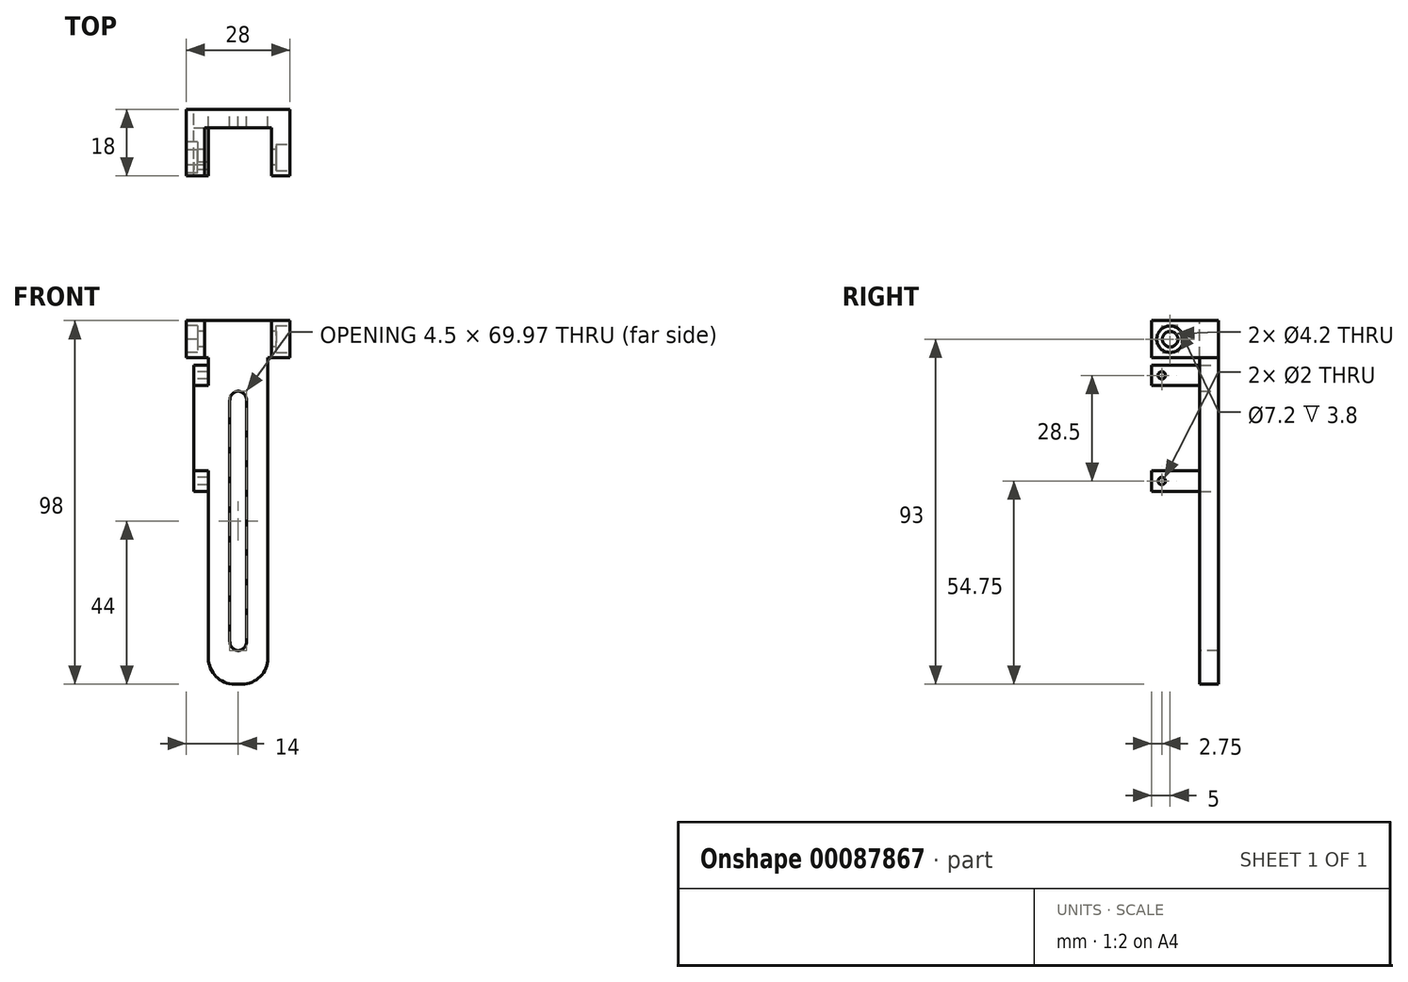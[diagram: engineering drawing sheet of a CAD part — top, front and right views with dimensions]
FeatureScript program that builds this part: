
annotation { "Feature Type Name" : "Feature", "Feature Type Description" : "" }
export const myFeature = defineFeature(function(context is Context, id is Id, definition is map)
    precondition{}
    {
        {
            var Q0;
            Q0=qCreatedBy(makeId("Front.planeOp"),FACE);
            var sketch = newSketch(context, id + "F0", { "sketchPlane" : qUnion([Q0])});
            skLineSegment(sketch, "E0.bottom", {"start": v(8, -44) * mm, "end": v(-8, -44) * mm});
            skLineSegment(sketch, "E0.top", {"start": v(8, 44) * mm, "end": v(-8, 44) * mm});
            skLineSegment(sketch, "E0.left", {"start": v(8, -44) * mm, "end": v(8, 44) * mm});
            skLineSegment(sketch, "E0.right", {"start": v(-8, -44) * mm, "end": v(-8, 44) * mm});
            skPoint(sketch, "E0.middle", {"position": v(0, 0) * mm});
            skLineSegment(sketch, "E1.bottom", {"start": v(-8, 42) * mm, "end": v(-12, 42) * mm});
            skLineSegment(sketch, "E1.top", {"start": v(-8, 8) * mm, "end": v(-12, 8) * mm});
            skLineSegment(sketch, "E1.left", {"start": v(-8, 42) * mm, "end": v(-8, 8) * mm});
            skLineSegment(sketch, "E1.right", {"start": v(-12, 42) * mm, "end": v(-12, 8) * mm});
            skLineSegment(sketch, "E2.bottom", {"start": v(14, 44) * mm, "end": v(8, 44) * mm});
            skLineSegment(sketch, "E2.top", {"start": v(14, 54) * mm, "end": v(-14, 54) * mm});
            skLineSegment(sketch, "E2.left", {"start": v(14, 44) * mm, "end": v(14, 54) * mm});
            skLineSegment(sketch, "E2.right", {"start": v(-14, 44) * mm, "end": v(-14, 54) * mm});
            skLineSegment(sketch, "E3.bottom", {"start": v(2.25, -35) * mm, "end": v(-2.25, -35) * mm});
            skLineSegment(sketch, "E3.top", {"start": v(2.25, 35) * mm, "end": v(-2.25, 35) * mm});
            skLineSegment(sketch, "E3.left", {"start": v(2.25, -35) * mm, "end": v(2.25, 35) * mm});
            skLineSegment(sketch, "E3.right", {"start": v(-2.25, -35) * mm, "end": v(-2.25, 35) * mm});
            skPoint(sketch, "E4", {"position": v(0, 54) * mm});
            skLineSegment(sketch, "E5.trimOffspring", {"start": v(-8, 44) * mm, "end": v(-14, 44) * mm});
            skSolve(sketch);
        }
        {
            var Q0;
            {var subQ1=sQuery(id+"F0.wireOp",EDGE,"E0.bottom");Q0=makeQuery(id+"F0.imprint","IMPRINT",FACE,{"disambiguationData":[TD([[makeQuery(id+"F0.imprint","IMPRINT",EDGE,{"derivedFrom":subQ1}),-1.0]])]});}
            var Q1;
            Q1=makeQuery(id+"F0.imprint","IMPRINT",FACE,{"disambiguationData":[TD([[makeQuery(id+"F0.imprint","IMPRINT",EDGE,{"derivedFrom":sQuery(id+"F0.wireOp",EDGE,"E0.top")}),-1.0]])]});
            var Q2;
            Q2=makeQuery(id+"F0.imprint","IMPRINT",FACE,{"disambiguationData":[TD([[makeQuery(id+"F0.imprint","IMPRINT",EDGE,{"derivedFrom":sQuery(id+"F0.wireOp",EDGE,"E1.bottom")}),1.0]])]});
            extrude(context, id + "F1", {"entities" : qUnion([Q0, Q1, Q2]), "depth" : 5 * mm});
        }
        {
            var Q0;
            Q0=makeQuery(id+"F1.opExtrude","CAP_FACE",FACE,{"disambiguationData":[OSD([sQuery(id+"F0.wireOp",EDGE,"E0.bottom"),sQuery(id+"F0.wireOp",EDGE,"E0.left"),sQuery(id+"F0.wireOp",EDGE,"E0.right"),sQuery(id+"F0.wireOp",EDGE,"E1.bottom"),sQuery(id+"F0.wireOp",EDGE,"E1.top"),sQuery(id+"F0.wireOp",EDGE,"E1.right"),sQuery(id+"F0.wireOp",EDGE,"E2.bottom"),sQuery(id+"F0.wireOp",EDGE,"E2.top"),sQuery(id+"F0.wireOp",EDGE,"E2.left"),sQuery(id+"F0.wireOp",EDGE,"E2.right"),sQuery(id+"F0.wireOp",EDGE,"E3.bottom"),sQuery(id+"F0.wireOp",EDGE,"E3.top"),sQuery(id+"F0.wireOp",EDGE,"E3.left"),sQuery(id+"F0.wireOp",EDGE,"E3.right"),sQuery(id+"F0.wireOp",EDGE,"E5.trimOffspring")])],"isStart":false});
            var sketch = newSketch(context, id + "F2", { "sketchPlane" : qUnion([Q0])});
            skLineSegment(sketch, "E6.bottom", {"start": v(14, 44) * mm, "end": v(9, 44) * mm});
            skLineSegment(sketch, "E6.top", {"start": v(14, 54) * mm, "end": v(9, 54) * mm});
            skLineSegment(sketch, "E6.left", {"start": v(14, 44) * mm, "end": v(14, 54) * mm});
            skLineSegment(sketch, "E6.right", {"start": v(9, 44) * mm, "end": v(9, 54) * mm});
            skLineSegment(sketch, "E7.bottom", {"start": v(-14, 44) * mm, "end": v(-9, 44) * mm});
            skLineSegment(sketch, "E7.top", {"start": v(-14, 54) * mm, "end": v(-9, 54) * mm});
            skLineSegment(sketch, "E7.left", {"start": v(-14, 44) * mm, "end": v(-14, 54) * mm});
            skLineSegment(sketch, "E7.right", {"start": v(-9, 44) * mm, "end": v(-9, 54) * mm});
            skLineSegment(sketch, "E8.bottom", {"start": v(-12, 8) * mm, "end": v(-8, 8) * mm});
            skLineSegment(sketch, "E8.top", {"start": v(-12, 13.5) * mm, "end": v(-8, 13.5) * mm});
            skLineSegment(sketch, "E8.left", {"start": v(-12, 8) * mm, "end": v(-12, 13.5) * mm});
            skLineSegment(sketch, "E8.right", {"start": v(-8, 8) * mm, "end": v(-8, 13.5) * mm});
            skLineSegment(sketch, "E9.bottom", {"start": v(-12, 42) * mm, "end": v(-8, 42) * mm});
            skLineSegment(sketch, "E9.top", {"start": v(-12, 36.5) * mm, "end": v(-8, 36.5) * mm});
            skLineSegment(sketch, "E9.left", {"start": v(-12, 42) * mm, "end": v(-12, 36.5) * mm});
            skLineSegment(sketch, "E9.right", {"start": v(-8, 42) * mm, "end": v(-8, 36.5) * mm});
            skSolve(sketch);
        }
        {
            var Q0;
            Q0 = qSketchRegion(id + "F2", true);
            extrude(context, id + "F3", {"entities" : qUnion([Q0]), "operationType" : NewBodyOperationType.ADD, "depth" : 13 * mm});
        }
        {
            var Q0;
            Q0=makeQuery(id+"F3.boolean.opBoolean","MERGE",FACE,{"derivedFrom":[makeQuery(id+"F1.opExtrude","SWEPT_FACE",FACE,{"disambiguationData":[OSD([sQuery(id+"F0.wireOp",EDGE,"E2.right")])]}),makeQuery(id+"F3.opExtrude","SWEPT_FACE",FACE,{"disambiguationData":[OSD([sQuery(id+"F2.wireOp",EDGE,"E7.left")])]})]});
            var sketch = newSketch(context, id + "F4", { "sketchPlane" : qUnion([Q0])});
            skLineSegment(sketch, "E10", {"start": v(0, 49) * mm, "end": v(18, 49) * mm, "construction": true});
            skCircle(sketch, "E11", {"center": v(13, 49) * mm, "radius": 2.1 * mm});
            skLineSegment(sketch, "E12.0.0", {"start": v(0, 42) * mm, "end": v(0, 8) * mm, "construction": true});
            skLineSegment(sketch, "E12.0.1", {"start": v(0, 8) * mm, "end": v(18, 8) * mm, "construction": true});
            skLineSegment(sketch, "E12.0.2", {"start": v(18, 8) * mm, "end": v(18, 13.5) * mm, "construction": true});
            skLineSegment(sketch, "E12.0.3", {"start": v(18, 13.5) * mm, "end": v(5, 13.5) * mm, "construction": true});
            skLineSegment(sketch, "E12.0.4", {"start": v(5, 13.5) * mm, "end": v(5, 36.5) * mm, "construction": true});
            skLineSegment(sketch, "E12.0.5", {"start": v(5, 36.5) * mm, "end": v(18, 36.5) * mm, "construction": true});
            skLineSegment(sketch, "E12.0.6", {"start": v(18, 36.5) * mm, "end": v(18, 42) * mm, "construction": true});
            skLineSegment(sketch, "E12.0.7", {"start": v(18, 42) * mm, "end": v(0, 42) * mm, "construction": true});
            skLineSegment(sketch, "E13", {"start": v(18, 39.25) * mm, "end": v(0, 39.25) * mm, "construction": true});
            skLineSegment(sketch, "E14", {"start": v(18, 10.75) * mm, "end": v(0, 10.75) * mm, "construction": true});
            skCircle(sketch, "E15", {"center": v(15.25, 39.25) * mm, "radius": 1 * mm});
            skCircle(sketch, "E16", {"center": v(15.25, 10.75) * mm, "radius": 1 * mm});
            skSolve(sketch);
        }
        {
            var Q0;
            Q0=makeQuery(id+"F4.imprint","IMPRINT",FACE,{"disambiguationData":[TD([[makeQuery(id+"F4.imprint","IMPRINT",EDGE,{"derivedFrom":sQuery(id+"F4.wireOp",EDGE,"E11")}),1.0]])]});
            var Q1;
            Q1=makeQuery(id+"F4.imprint","IMPRINT",FACE,{"disambiguationData":[TD([[makeQuery(id+"F4.imprint","IMPRINT",EDGE,{"derivedFrom":sQuery(id+"F4.wireOp",EDGE,"E15")}),1.0]])]});
            var Q2;
            Q2=makeQuery(id+"F4.imprint","IMPRINT",FACE,{"disambiguationData":[TD([[makeQuery(id+"F4.imprint","IMPRINT",EDGE,{"derivedFrom":sQuery(id+"F4.wireOp",EDGE,"E16")}),1.0]])]});
            extrude(context, id + "F5", {"entities" : qUnion([Q0, Q1, Q2]), "operationType" : NewBodyOperationType.REMOVE, "endBound" : BoundingType.THROUGH_ALL, "oppositeDirection" : true, "depth" : 25 * mm});
        }
        {
            var Q0;
            Q0=makeQuery(id+"F3.boolean.opBoolean","MERGE",FACE,{"derivedFrom":[makeQuery(id+"F1.opExtrude","SWEPT_FACE",FACE,{"disambiguationData":[OSD([sQuery(id+"F0.wireOp",EDGE,"E2.right")])]}),makeQuery(id+"F3.opExtrude","SWEPT_FACE",FACE,{"disambiguationData":[OSD([sQuery(id+"F2.wireOp",EDGE,"E7.left")])]})]});
            var sketch = newSketch(context, id + "F6", { "sketchPlane" : qUnion([Q0])});
            skCircle(sketch, "E17.cCircle", {"center": v(13, 49) * mm, "radius": 4.16 * mm, "construction": true});
            skPoint(sketch, "E17.cCircle.perimeterSnap0", {"position": v(18, 49) * mm});
            skLineSegment(sketch, "E17.0", {"start": v(17.16, 49) * mm, "end": v(15.08, 45.4) * mm});
            skPoint(sketch, "E17.0.startSnap0", {"position": v(18, 49) * mm});
            skLineSegment(sketch, "E17.1", {"start": v(15.08, 45.4) * mm, "end": v(10.92, 45.4) * mm});
            skLineSegment(sketch, "E17.2", {"start": v(10.92, 45.4) * mm, "end": v(8.84, 49) * mm});
            skLineSegment(sketch, "E17.3", {"start": v(8.84, 49) * mm, "end": v(10.92, 52.6) * mm});
            skLineSegment(sketch, "E17.4", {"start": v(10.92, 52.6) * mm, "end": v(15.08, 52.6) * mm});
            skLineSegment(sketch, "E17.5", {"start": v(15.08, 52.6) * mm, "end": v(17.16, 49) * mm});
            skSolve(sketch);
        }
        {
            var Q0;
            Q0=makeQuery(id+"F6.imprint","IMPRINT",FACE,{"disambiguationData":[TD([[makeQuery(id+"F6.imprint","IMPRINT",EDGE,{"derivedFrom":sQuery(id+"F6.wireOp",EDGE,"E17.0")}),-1.0]])]});
            extrude(context, id + "F7", {"entities" : qUnion([Q0]), "operationType" : NewBodyOperationType.REMOVE, "oppositeDirection" : true, "depth" : 3 * mm});
        }
        {
            var Q0;
            Q0=makeQuery(id+"F3.boolean.opBoolean","MERGE",FACE,{"derivedFrom":[makeQuery(id+"F1.opExtrude","SWEPT_FACE",FACE,{"disambiguationData":[OSD([sQuery(id+"F0.wireOp",EDGE,"E2.left")])]}),makeQuery(id+"F3.opExtrude","SWEPT_FACE",FACE,{"disambiguationData":[OSD([sQuery(id+"F2.wireOp",EDGE,"E6.left")])]})]});
            var sketch = newSketch(context, id + "F8", { "sketchPlane" : qUnion([Q0])});
            skCircle(sketch, "E18", {"center": v(-13, 49) * mm, "radius": 3.6 * mm});
            skSolve(sketch);
        }
        {
            var Q0;
            Q0=makeQuery(id+"F8.imprint","IMPRINT",FACE,{"disambiguationData":[TD([[makeQuery(id+"F8.imprint","IMPRINT",EDGE,{"derivedFrom":sQuery(id+"F8.wireOp",EDGE,"E18")}),1.0]])]});
            extrude(context, id + "F9", {"entities" : qUnion([Q0]), "operationType" : NewBodyOperationType.REMOVE, "oppositeDirection" : true, "depth" : 3.8 * mm});
        }
        {
            var Q0;
            Q0=makeQuery(id+"F1.opExtrude","SWEPT_EDGE",EDGE,{"disambiguationData":[OSD([sQuery(id+"F0.wireOp",EDGE,"E0.bottom"),sQuery(id+"F0.wireOp",EDGE,"E0.left")])]});
            var Q1;
            Q1=makeQuery(id+"F1.opExtrude","SWEPT_EDGE",EDGE,{"disambiguationData":[OSD([sQuery(id+"F0.wireOp",EDGE,"E0.bottom"),sQuery(id+"F0.wireOp",EDGE,"E0.right")])]});
            fillet(context, id + "F10", {"entities" : qUnion([Q0, Q1]), "radius" : 7 * mm, "tangentPropagation" : true, "allowEdgeOverflow" : false});
        }
        {
            var Q0;
            Q0=makeQuery(id+"F1.opExtrude","SWEPT_EDGE",EDGE,{"disambiguationData":[OSD([sQuery(id+"F0.wireOp",EDGE,"E3.bottom"),sQuery(id+"F0.wireOp",EDGE,"E3.right")])]});
            var Q1;
            Q1=makeQuery(id+"F1.opExtrude","SWEPT_EDGE",EDGE,{"disambiguationData":[OSD([sQuery(id+"F0.wireOp",EDGE,"E3.bottom"),sQuery(id+"F0.wireOp",EDGE,"E3.left")])]});
            var Q2;
            Q2=makeQuery(id+"F1.opExtrude","SWEPT_EDGE",EDGE,{"disambiguationData":[OSD([sQuery(id+"F0.wireOp",EDGE,"E3.top"),sQuery(id+"F0.wireOp",EDGE,"E3.right")])]});
            var Q3;
            Q3=makeQuery(id+"F1.opExtrude","SWEPT_EDGE",EDGE,{"disambiguationData":[OSD([sQuery(id+"F0.wireOp",EDGE,"E3.top"),sQuery(id+"F0.wireOp",EDGE,"E3.left")])]});
            fillet(context, id + "F11", {"entities" : qUnion([Q0, Q1, Q2, Q3]), "radius" : 2.5 * mm, "tangentPropagation" : true, "allowEdgeOverflow" : false});
        }
    });
